# Revit family: IS_Tempo_E3243_BIM_GB
name_source: partatom
category: Plumbing Fixtures
revit_build: Autodesk Revit MEP 2012 (Build: 20110309_2315(x64)
units: mm (PartAtom-declared; Revit-internal decimal feet)

## types (2) — shared parameters
Accessories = www.idealspec.co.uk
AreaUnits = millimeters
Assembly Code = C1030200
AssetType = Fixed
BREEAM = No
Brand = Ideal Standard
Default Elevation = 1800 mm  [stored 5.90551 ft]
Description = Tempo 300 x 235 x 1500mm Column Unit With 2 Doors
DurationUnit = year
ECA = No
ExpectedLife = 30
Features = 2 doors
Handles = ISI_IdealStandard_Handles_Silver_Render
IfcExportAs = IfcFurnitureType
IfcExportType = USERDEFINED
InstallationInstructions = www.idealspec.co.uk/resources.html
LinearUnits = millimeters
MainColor = White
ManufacturerURL = www.specifysottini.co.uk
Material = Laminated board
ModelReference = Tempo 300 x 235 x 1500mm Column Unit With 2 Doors
NBSDescription = Bathroom integrated duct work
NBSReference = 45-35-72/320
NominalDepth = 235 mm  [stored 0.770997 ft]
NominalHeight = 1500 mm  [stored 4.92126 ft]
NominalLength = 235 mm  [stored 0.770997 ft]
NominalWidth = 300 mm  [stored 0.984252 ft]
Shape = Rectangular
Size = 1500 x 300 x 235 mm
Space = Internal
SpareParts = www.fastpart-spares.co.uk
TMV3 = No
URL = www.idealspec.co.uk
Uniclass2 = Pr_40_30_78_04
Version = 1
VolumeUnits = Litres
WRAS = No
WarrantyDescription = Manufacturers warranty
WarrantyDurationParts = 5
WarrantyDurationUnit = year
WaterEfficientProduct = No
zero-valued in all types: CWFU, HWFU, WFU

## per-type parameters (varying)
| type | BIMObjectName | Color | Finish | Laminate | Model | ModelNumber | Name | ProductInformation |
| E3243WG - Tempo 300 x 235 x 1500mm Column Unit With 2 Doors - Gloss White | ISI_IdealStandard_Furniture_Tempo_E3243WG | GlossWhite | GlossWhite | ISI_IdealStandard_Laminate_WhiteGloss_Render | E3243WG | E3243WG | Furniture_Tempo_E3243WG_IdealStandard | www.idealspec.co.uk/assets/datasheet/E3243WG |
| E3243SG - Tempo 300 x 235 x 1500mm Column Unit With 2 Doors - Sandy grey | ISI_IdealStandard_Furniture_Tempo_E3243SG | Sandy Grey | Sandy Grey | ISI_IdealStandard_Laminate_SandyGrey_Render | E3243SG | E3243SG | Furniture_Tempo_E3243SG_IdealStandard | www.idealspec.co.uk/assets/datasheet/E3243SG |

note: [stored X ft] marks values corroborated as IEEE doubles in the binary element streams (Revit-internal decimal feet)

## geometry (parser evidence)
native form markers: Blend x8, Sweep x3
no freeform markers — native parametric forms only
